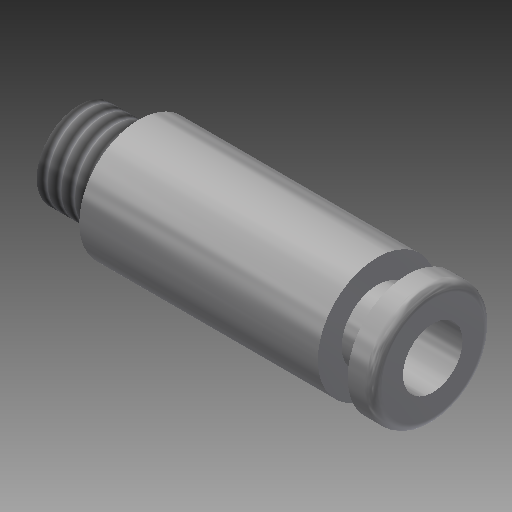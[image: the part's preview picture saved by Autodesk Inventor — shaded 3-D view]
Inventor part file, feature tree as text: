
AUTODESK INVENTOR PART (.ipt)
format: ipt  version: 2018 (Build 220112000, 112)  size: 208,896 bytes
history: native  units: mm
features: revolve x1, thread x1, fillet x1
ambient origin geometry x8: Origin, YZ Plane, XZ Plane, XY Plane, X Axis, Y Axis, Z Axis, Center Point
bodies: Volumenkörper1 (feature_tree)
feature tree (3):
  revolve  "Umdrehung1"
  thread  "Gewinde1"  [1 undecoded]
  fillet  "Rundung1"  Radius=3.5mm
note: 1 required parameter value undecoded (feature->parameter linkage not recoverable at this tier; creation-order binding heuristic only, values carry confidence <= 0.55)
